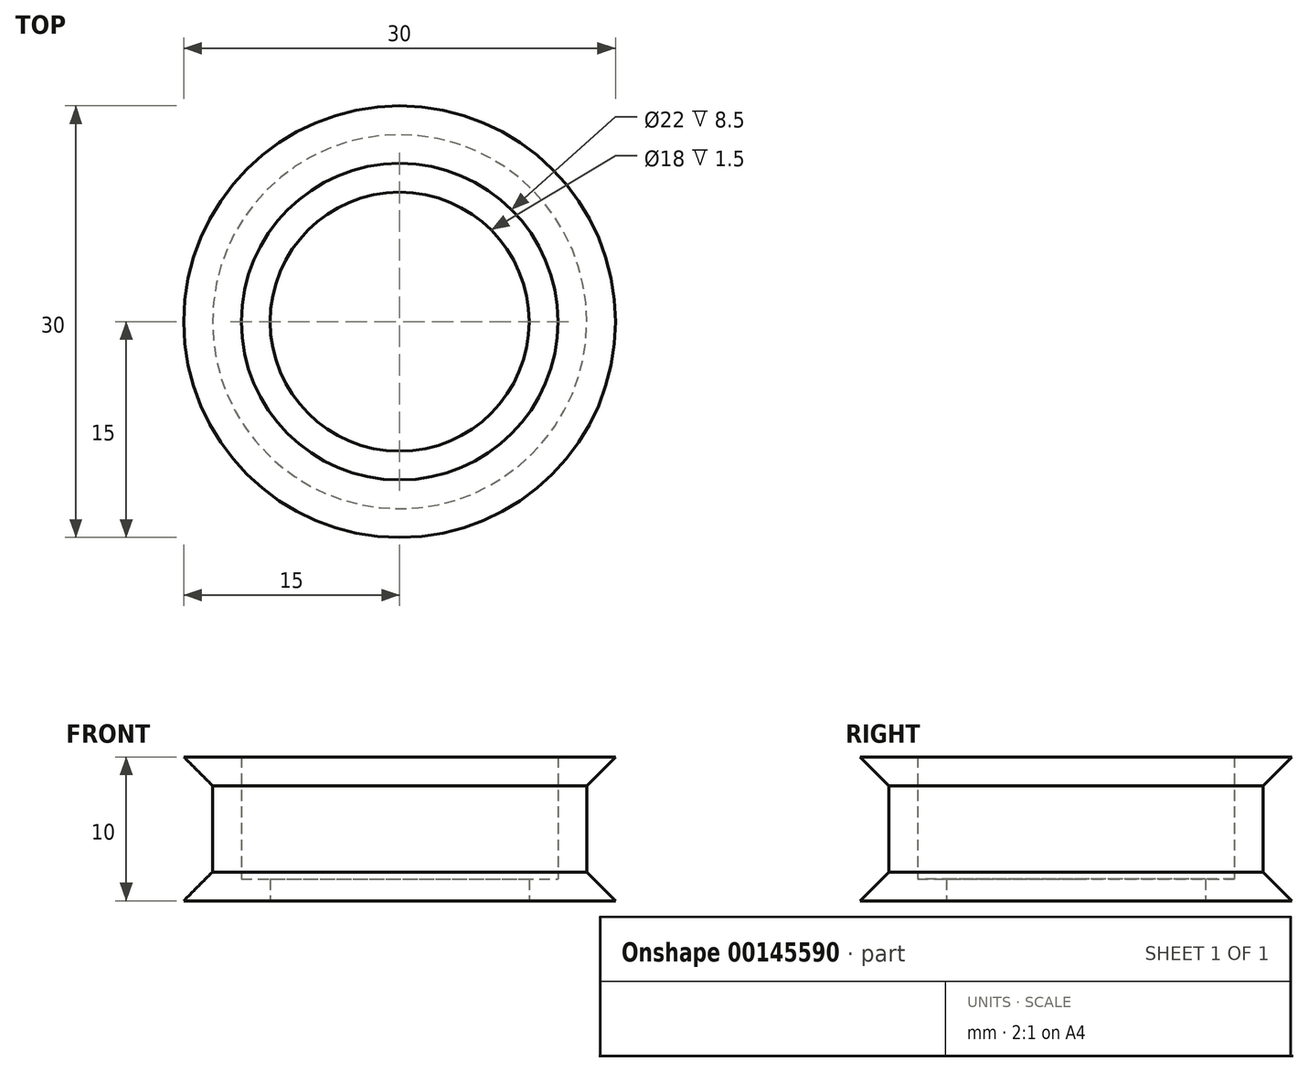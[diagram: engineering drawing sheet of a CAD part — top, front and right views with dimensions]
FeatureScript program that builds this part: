
annotation { "Feature Type Name" : "Feature", "Feature Type Description" : "" }
export const myFeature = defineFeature(function(context is Context, id is Id, definition is map)
    precondition{}
    {
        {
            var Q0;
            Q0=qCreatedBy(makeId("Front.planeOp"),FACE);
            var sketch = newSketch(context, id + "F0", { "sketchPlane" : qUnion([Q0])});
            skLineSegment(sketch, "E0", {"start": v(11, 4.8) * mm, "end": v(15, 4.8) * mm});
            skLineSegment(sketch, "E1", {"start": v(15, 4.8) * mm, "end": v(13, 2.8) * mm});
            skLineSegment(sketch, "E2", {"start": v(13, 2.8) * mm, "end": v(13, -3.2) * mm});
            skLineSegment(sketch, "E3", {"start": v(13, -3.2) * mm, "end": v(15, -5.2) * mm});
            skLineSegment(sketch, "E4", {"start": v(15, -5.2) * mm, "end": v(11, -5.2) * mm});
            skLineSegment(sketch, "E5", {"start": v(11, -5.2) * mm, "end": v(11, 4.8) * mm});
            skLineSegment(sketch, "E6", {"start": v(0, -3.77) * mm, "end": v(0, 4.95) * mm, "construction": true});
            skLineSegment(sketch, "E7.bottom", {"start": v(11, -5.2) * mm, "end": v(9, -5.2) * mm});
            skLineSegment(sketch, "E7.top", {"start": v(11, -3.7) * mm, "end": v(9, -3.7) * mm});
            skLineSegment(sketch, "E7.left", {"start": v(11, -5.2) * mm, "end": v(11, -3.7) * mm});
            skLineSegment(sketch, "E7.right", {"start": v(9, -5.2) * mm, "end": v(9, -3.7) * mm});
            skSolve(sketch);
        }
        {
            var Q0;
            Q0=qSketchRegion(id+"F0",true);
            var Q1;
            Q1=sQuery(id+"F0.wireOp",EDGE,"E6");
            revolve(context, id + "F1", {"entities" : qUnion([Q0]), "axis" : qUnion([Q1]), "revolveType" : RevolveType.FULL});
        }
    });
